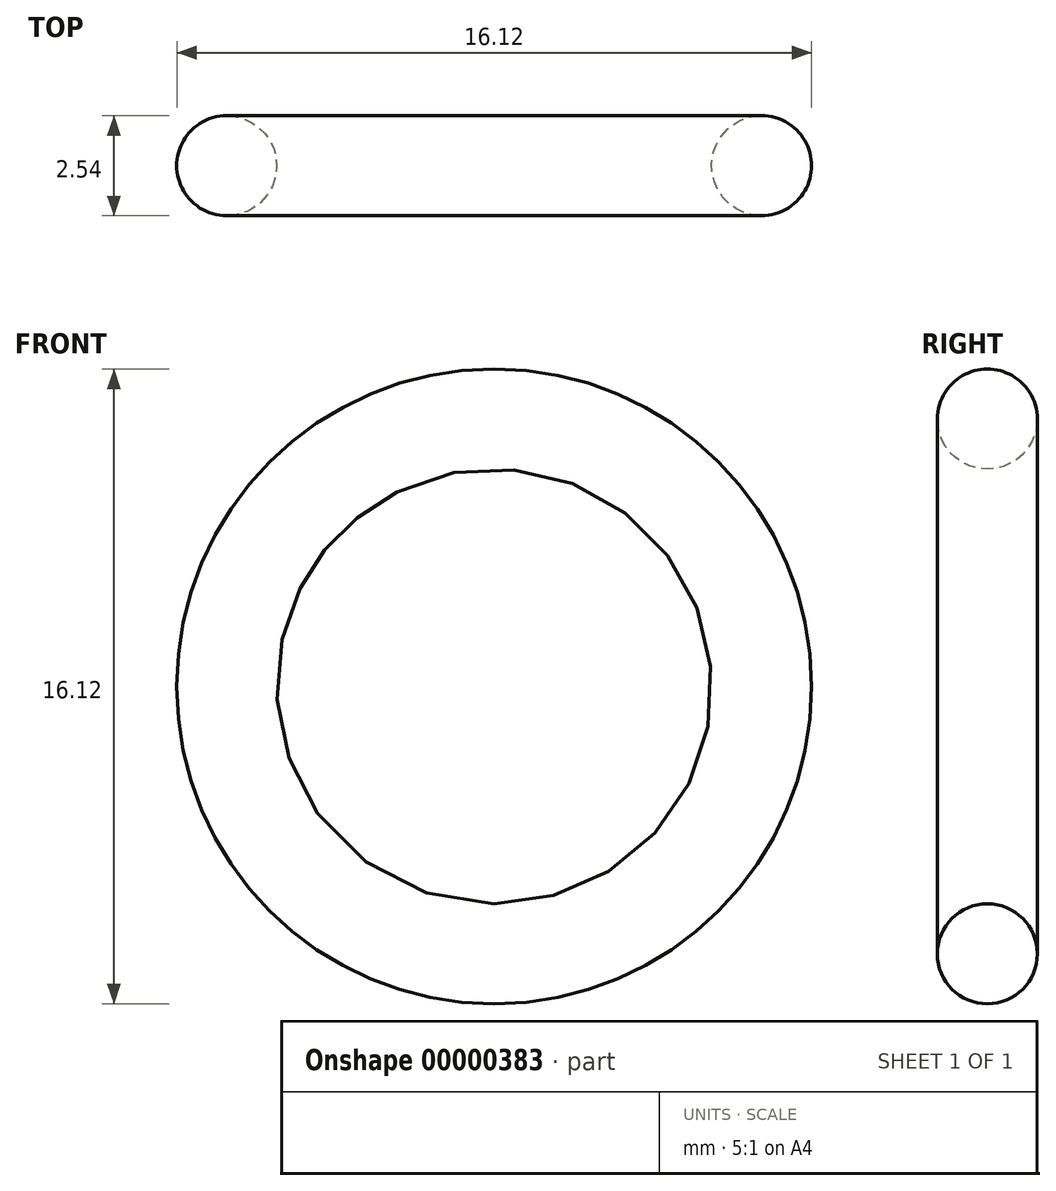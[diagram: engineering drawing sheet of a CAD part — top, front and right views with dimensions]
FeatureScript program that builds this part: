
annotation { "Feature Type Name" : "Feature", "Feature Type Description" : "" }
export const myFeature = defineFeature(function(context is Context, id is Id, definition is map)
    precondition{}
    {
        {
            var Q0;
            Q0=qCreatedBy(makeId("Top.planeOp"),FACE);
            var sketch = newSketch(context, id + "F0", { "sketchPlane" : qUnion([Q0])});
            skCircle(sketch, "E0", {"center": v(6.8, 0) * mm, "radius": 1.27 * mm});
            skLineSegment(sketch, "E1", {"start": v(0, 0) * mm, "end": v(0, 3.47) * mm, "construction": true});
            skSolve(sketch);
        }
        {
            var Q0;
            Q0=makeQuery(id+"F0.imprint","IMPRINT",FACE,{"disambiguationData":[TD([[makeQuery(id+"F0.imprint","IMPRINT",EDGE,{"derivedFrom":sQuery(id+"F0.wireOp",EDGE,"E0")}),1.0]])]});
            var Q1;
            Q1=sQuery(id+"F0.wireOp",EDGE,"E1");
            revolve(context, id + "F1", {"entities" : qUnion([Q0]), "axis" : qUnion([Q1]), "revolveType" : RevolveType.FULL});
        }
    });
